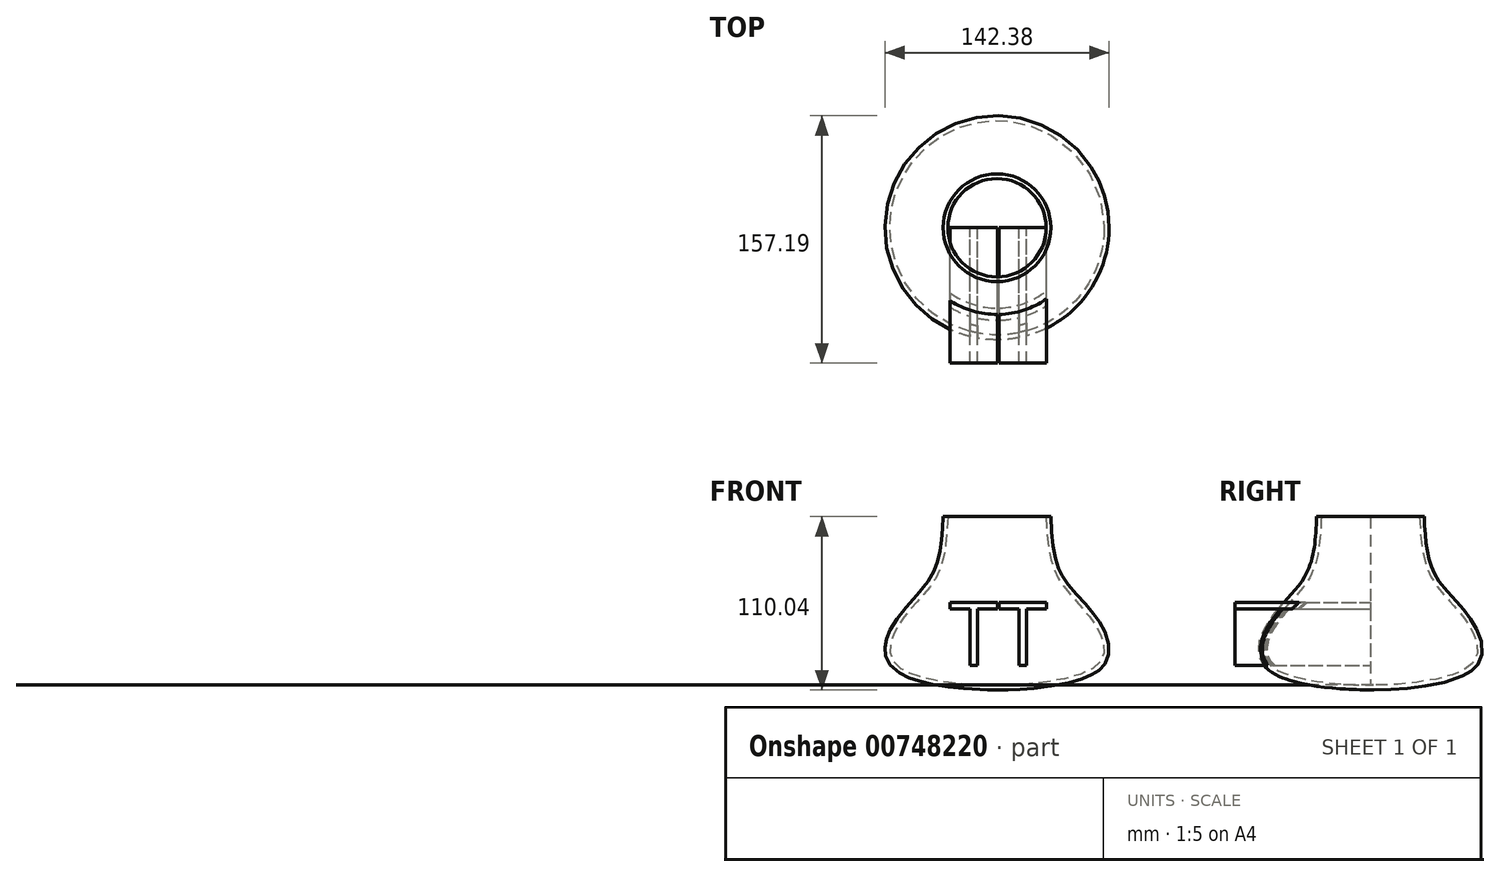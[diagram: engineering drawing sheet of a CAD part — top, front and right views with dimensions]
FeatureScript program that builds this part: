
annotation { "Feature Type Name" : "Feature", "Feature Type Description" : "" }
export const myFeature = defineFeature(function(context is Context, id is Id, definition is map)
    precondition{}
    {
        {
            var Q0;
            Q0=qCreatedBy(makeId("Front.planeOp"),FACE);
            var sketch = newSketch(context, id + "F0", { "sketchPlane" : qUnion([Q0])});
            skFitSpline(sketch, "E0", {"points": [v(31.06, 45.4) * mm, v(37.8, 3.51) * mm, v(60.85, -25.72) * mm, v(62.26, -54.95) * mm, v(-10.26, -65.35) * mm, v(-9.98, -64.5) * mm], "startDerivative": vector(6.18, -192.35) * mm, "endDerivative": vector(26.17, 25.7) * mm});
            skLineSegment(sketch, "E1", {"start": v(0, 58.04) * mm, "end": v(0, -71.25) * mm});
            skFitSpline(sketch, "E2.0", {"points": [v(34.06, 45.5) * mm, v(34.19, 41.48) * mm, v(34.38, 35.5) * mm, v(34.92, 27.82) * mm, v(35.54, 22.26) * mm, v(36.43, 16.94) * mm, v(37.45, 12.76) * mm, v(38.47, 9.6) * mm, v(39.34, 7.32) * mm, v(40.15, 5.5) * mm, v(40.87, 4.1) * mm, v(42, 2.03) * mm, v(43.95, -0.96) * mm, v(46.96, -4.82) * mm, v(50.3, -8.64) * mm, v(53.84, -12.51) * mm, v(57.46, -16.55) * mm, v(60.45, -20.14) * mm, v(62.76, -23.2) * mm, v(64.43, -25.6) * mm, v(66, -28.1) * mm, v(67.94, -31.56) * mm, v(69.92, -36.07) * mm, v(71.03, -40.76) * mm, v(71.15, -44.58) * mm, v(70.8, -47.44) * mm, v(69.92, -50.25) * mm, v(68.48, -52.93) * mm, v(66.8, -54.98) * mm, v(65.17, -56.5) * mm, v(63.81, -57.56) * mm, v(62.33, -58.55) * mm, v(60.2, -59.78) * mm, v(57.28, -61.17) * mm, v(53.4, -62.63) * mm, v(47.8, -64.34) * mm, v(40.14, -66.07) * mm, v(30.38, -67.6) * mm, v(22.2, -68.47) * mm, v(15.87, -68.94) * mm, v(11.3, -69.2) * mm, v(6.99, -69.35) * mm, v(2.98, -69.42) * mm, v(-0.06, -69.4) * mm, v(-2.27, -69.35) * mm, v(-3.81, -69.3) * mm, v(-5.24, -69.22) * mm, v(-6.54, -69.12) * mm, v(-7.7, -69) * mm, v(-8.58, -68.9) * mm, v(-9.22, -68.8) * mm, v(-9.67, -68.7) * mm, v(-10.1, -68.6) * mm, v(-10.53, -68.5) * mm, v(-10.96, -68.35) * mm, v(-11.43, -68.15) * mm, v(-11.88, -67.9) * mm, v(-12.32, -67.54) * mm, v(-12.66, -67.2) * mm, v(-12.98, -66.74) * mm, v(-13.23, -66.18) * mm, v(-13.38, -65.57) * mm, v(-13.4, -64.97) * mm, v(-13.34, -64.44) * mm, v(-13.17, -63.85) * mm, v(-12.9, -63.33) * mm, v(-12.61, -62.93) * mm, v(-12.38, -62.67) * mm, v(-12.2, -62.48) * mm, v(-12.11, -62.4) * mm, v(-12.08, -62.37) * mm]});
            skLineSegment(sketch, "E3", {"start": v(20.94, 40.62) * mm, "end": v(44.55, 40.62) * mm});
            skSolve(sketch);
        }
        {
            var Q0;
            {var subQ0=sQuery(id+"F0.wireOp",EDGE,"E1");var subQ1=sQuery(id+"F0.wireOp",EDGE,"E0");var subQ2=makeQuery(id+"F0.imprint","INTERSECT",VERTEX,{"derivedFrom":[subQ1,subQ0]});Q0=makeQuery(id+"F0.imprint","IMPRINT",FACE,{"disambiguationData":[TD([[makeQuery(id+"F0.imprint","IMPRINT",EDGE,{"disambiguationData":[TD([[subQ2,1.0]])],"derivedFrom":subQ1}),1.0]])]});}
            var Q1;
            Q1=sQuery(id+"F0.wireOp",EDGE,"E1");
            revolve(context, id + "F1", {"surfaceOperationType" : NewSurfaceOperationType.NEW, "entities" : qUnion([Q0]), "axis" : qUnion([Q1]), "revolveType" : RevolveType.FULL});
        }
        {
            var Q0;
            Q0=qCreatedBy(makeId("Front.planeOp"),FACE);
            var sketch = newSketch(context, id + "F2", { "sketchPlane" : qUnion([Q0])});
            skText(sketch, "E4", { "text": "TT", "fontName": "OpenSans-Regular.ttf"});
            const initialGuessF2  = {"E4": [-0.03025, -0.05398, 1, 0, 0.04045]};
            skSetInitialGuess(sketch, initialGuessF2);
            skSolve(sketch);
        }
        {
            var Q0;
            Q0 = qSketchRegion(id + "F2", true);
            extrude(context, id + "F3", {"entities" : qUnion([Q0]), "operationType" : NewBodyOperationType.ADD, "depth" : 86 * mm, "offsetDistance" : 25 * mm});
        }
    });
